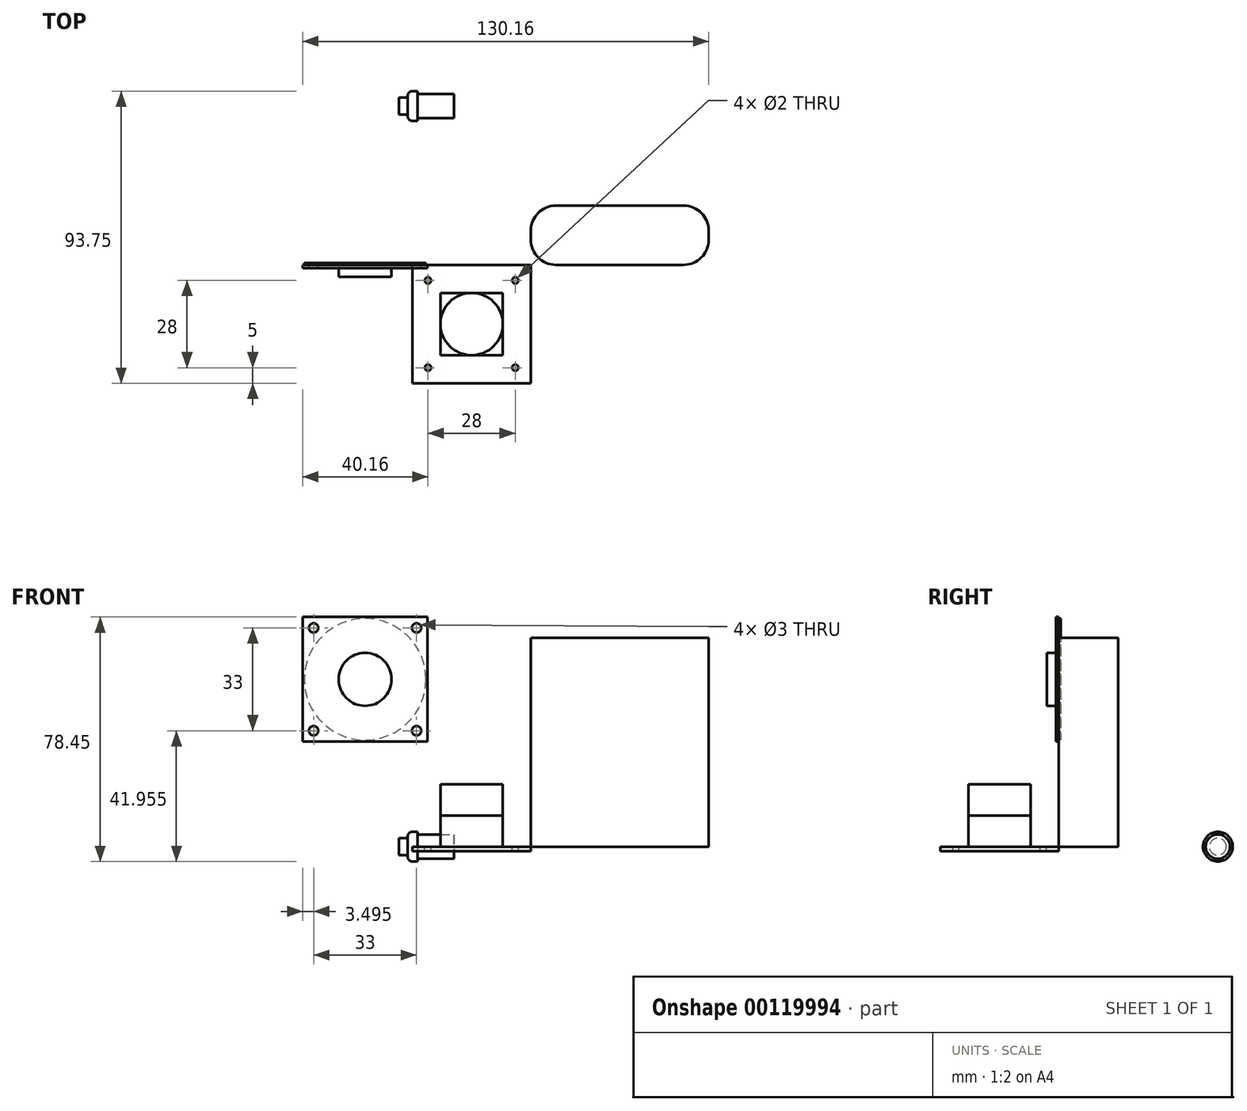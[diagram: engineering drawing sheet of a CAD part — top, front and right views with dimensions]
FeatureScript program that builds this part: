
annotation { "Feature Type Name" : "Feature", "Feature Type Description" : "" }
export const myFeature = defineFeature(function(context is Context, id is Id, definition is map)
    precondition{}
    {
        {
            var Q0;
            Q0=qCreatedBy(makeId("Top.planeOp"),FACE);
            var sketch = newSketch(context, id + "F0", { "sketchPlane" : qUnion([Q0])});
            skLineSegment(sketch, "E0.bottom", {"start": v(8, 0) * mm, "end": v(49, 0) * mm});
            skLineSegment(sketch, "E0.top", {"start": v(8, 19) * mm, "end": v(49, 19) * mm});
            skLineSegment(sketch, "E0.left", {"start": v(0, 8) * mm, "end": v(0, 11) * mm});
            skLineSegment(sketch, "E0.right", {"start": v(57, 8) * mm, "end": v(57, 11) * mm});
            skPoint(sketch, "E1.visualSharp", {"position": v(0, 19) * mm});
            skArc(sketch, "E1.filletArc", {"start": v(8, 19) * mm, "mid": v(2.34, 16.66) * mm, "end": v(0, 11) * mm});
            skPoint(sketch, "E2.visualSharp", {"position": v(0, 0) * mm});
            skArc(sketch, "E2.filletArc", {"start": v(0, 8) * mm, "mid": v(2.34, 2.34) * mm, "end": v(8, 0) * mm});
            skPoint(sketch, "E3.visualSharp", {"position": v(57, 19) * mm});
            skArc(sketch, "E3.filletArc", {"start": v(57, 11) * mm, "mid": v(54.66, 16.66) * mm, "end": v(49, 19) * mm});
            skPoint(sketch, "E4.visualSharp", {"position": v(57, 0) * mm});
            skArc(sketch, "E4.filletArc", {"start": v(49, 0) * mm, "mid": v(54.66, 2.34) * mm, "end": v(57, 8) * mm});
            skSolve(sketch);
        }
        {
            var Q0;
            Q0=makeQuery(id+"F0.imprint","IMPRINT",FACE,{"disambiguationData":[TD([[makeQuery(id+"F0.imprint","IMPRINT",EDGE,{"derivedFrom":sQuery(id+"F0.wireOp",EDGE,"E0.bottom")}),1.0]])]});
            extrude(context, id + "F1", {"entities" : qUnion([Q0]), "depth" : 67 * mm});
        }
        {
            var Q0;
            Q0=qCreatedBy(makeId("Top.planeOp"),FACE);
            var sketch = newSketch(context, id + "F2", { "sketchPlane" : qUnion([Q0])});
            skLineSegment(sketch, "E5.bottom", {"start": v(0, 0) * mm, "end": v(-38, 0) * mm});
            skLineSegment(sketch, "E5.top", {"start": v(0, -38) * mm, "end": v(-38, -38) * mm});
            skLineSegment(sketch, "E5.left", {"start": v(0, 0) * mm, "end": v(0, -38) * mm});
            skLineSegment(sketch, "E5.right", {"start": v(-38, 0) * mm, "end": v(-38, -38) * mm});
            skLineSegment(sketch, "E6.bottom", {"start": v(-33, -5) * mm, "end": v(-5, -5) * mm, "construction": true});
            skLineSegment(sketch, "E6.top", {"start": v(-33, -33) * mm, "end": v(-5, -33) * mm, "construction": true});
            skLineSegment(sketch, "E6.left", {"start": v(-33, -5) * mm, "end": v(-33, -33) * mm, "construction": true});
            skLineSegment(sketch, "E6.right", {"start": v(-5, -5) * mm, "end": v(-5, -33) * mm, "construction": true});
            skPoint(sketch, "E6.middle", {"position": v(-19, -19) * mm});
            skPoint(sketch, "E6.middle.positionSnap0", {"position": v(-19, -38) * mm});
            skPoint(sketch, "E6.middle.positionSnap1", {"position": v(0, -19) * mm});
            skPoint(sketch, "E6.centerSnap0", {"position": v(-19, -38) * mm});
            skPoint(sketch, "E6.centerSnap1", {"position": v(0, -19) * mm});
            skLineSegment(sketch, "E7.bottom", {"start": v(-29, -9) * mm, "end": v(-9, -9) * mm});
            skLineSegment(sketch, "E7.top", {"start": v(-29, -29) * mm, "end": v(-9, -29) * mm});
            skLineSegment(sketch, "E7.left", {"start": v(-29, -9) * mm, "end": v(-29, -29) * mm});
            skLineSegment(sketch, "E7.right", {"start": v(-9, -9) * mm, "end": v(-9, -29) * mm});
            skCircle(sketch, "E8", {"center": v(-33, -5) * mm, "radius": 1 * mm});
            skCircle(sketch, "E9", {"center": v(-5, -5) * mm, "radius": 1 * mm});
            skCircle(sketch, "E10", {"center": v(-5, -33) * mm, "radius": 1 * mm});
            skCircle(sketch, "E11", {"center": v(-33, -33) * mm, "radius": 1 * mm});
            skCircle(sketch, "E12", {"center": v(-19, -19) * mm, "radius": 10 * mm});
            skSolve(sketch);
        }
        {
            var Q0;
            Q0 = qSketchRegion(id + "F2", true);
            var Q1;
            Q1=makeQuery(id+"F2.imprint","IMPRINT",FACE,{"disambiguationData":[TD([[makeQuery(id+"F2.imprint","IMPRINT",EDGE,{"derivedFrom":sQuery(id+"F2.wireOp",EDGE,"E7.bottom")}),-1.0]])]});
            var Q2;
            {var subQ0=sQuery(id+"F2.wireOp",EDGE,"E12");var subQ1=makeQuery(id+"F2.imprint","INTERSECT",VERTEX,{"derivedFrom":[sQuery(id+"F2.wireOp",EDGE,"E7.bottom"),subQ0]});Q2=makeQuery(id+"F2.imprint","IMPRINT",FACE,{"disambiguationData":[TD([[makeQuery(id+"F2.imprint","IMPRINT",EDGE,{"disambiguationData":[TD([[subQ1,1.0]])],"derivedFrom":subQ0}),1.0]])]});}
            var Q3;
            {var subQ0=sQuery(id+"F2.wireOp",EDGE,"E7.left");var subQ1=sQuery(id+"F2.wireOp",EDGE,"E7.top");var subQ2=makeQuery(id+"F2.imprint","INTERSECT",VERTEX,{"derivedFrom":[subQ1,subQ0]});Q3=makeQuery(id+"F2.imprint","IMPRINT",FACE,{"disambiguationData":[TD([[makeQuery(id+"F2.imprint","IMPRINT",EDGE,{"disambiguationData":[TD([[subQ2,-1.0]])],"derivedFrom":subQ1}),1.0]])]});}
            var Q4;
            {var subQ0=sQuery(id+"F2.wireOp",EDGE,"E7.right");var subQ1=sQuery(id+"F2.wireOp",EDGE,"E7.top");var subQ2=makeQuery(id+"F2.imprint","INTERSECT",VERTEX,{"derivedFrom":[subQ1,subQ0]});Q4=makeQuery(id+"F2.imprint","IMPRINT",FACE,{"disambiguationData":[TD([[makeQuery(id+"F2.imprint","IMPRINT",EDGE,{"disambiguationData":[TD([[subQ2,1.0]])],"derivedFrom":subQ1}),1.0]])]});}
            extrude(context, id + "F3", {"entities" : qUnion([Q0, Q1, Q2, Q3, Q4]), "oppositeDirection" : true, "depth" : 1.5 * mm});
        }
        {
            var Q0;
            Q0=makeQuery(id+"F2.imprint","IMPRINT",FACE,{"disambiguationData":[TD([[makeQuery(id+"F2.imprint","IMPRINT",EDGE,{"derivedFrom":sQuery(id+"F2.wireOp",EDGE,"E7.bottom")}),-1.0]])]});
            var Q1;
            {var subQ0=sQuery(id+"F2.wireOp",EDGE,"E7.left");var subQ1=sQuery(id+"F2.wireOp",EDGE,"E7.top");var subQ2=makeQuery(id+"F2.imprint","INTERSECT",VERTEX,{"derivedFrom":[subQ1,subQ0]});Q1=makeQuery(id+"F2.imprint","IMPRINT",FACE,{"disambiguationData":[TD([[makeQuery(id+"F2.imprint","IMPRINT",EDGE,{"disambiguationData":[TD([[subQ2,-1.0]])],"derivedFrom":subQ1}),1.0]])]});}
            var Q2;
            {var subQ0=sQuery(id+"F2.wireOp",EDGE,"E12");var subQ1=makeQuery(id+"F2.imprint","INTERSECT",VERTEX,{"derivedFrom":[sQuery(id+"F2.wireOp",EDGE,"E7.bottom"),subQ0]});Q2=makeQuery(id+"F2.imprint","IMPRINT",FACE,{"disambiguationData":[TD([[makeQuery(id+"F2.imprint","IMPRINT",EDGE,{"disambiguationData":[TD([[subQ1,1.0]])],"derivedFrom":subQ0}),1.0]])]});}
            var Q3;
            {var subQ0=sQuery(id+"F2.wireOp",EDGE,"E7.right");var subQ1=sQuery(id+"F2.wireOp",EDGE,"E7.top");var subQ2=makeQuery(id+"F2.imprint","INTERSECT",VERTEX,{"derivedFrom":[subQ1,subQ0]});Q3=makeQuery(id+"F2.imprint","IMPRINT",FACE,{"disambiguationData":[TD([[makeQuery(id+"F2.imprint","IMPRINT",EDGE,{"disambiguationData":[TD([[subQ2,1.0]])],"derivedFrom":subQ1}),1.0]])]});}
            extrude(context, id + "F4", {"entities" : qUnion([Q0, Q1, Q2, Q3]), "operationType" : NewBodyOperationType.ADD, "depth" : 10 * mm});
        }
        {
            var Q0;
            {var subQ0=sQuery(id+"F2.wireOp",EDGE,"E12");var subQ1=makeQuery(id+"F2.imprint","INTERSECT",VERTEX,{"derivedFrom":[sQuery(id+"F2.wireOp",EDGE,"E7.bottom"),subQ0]});Q0=makeQuery(id+"F2.imprint","IMPRINT",FACE,{"disambiguationData":[TD([[makeQuery(id+"F2.imprint","IMPRINT",EDGE,{"disambiguationData":[TD([[subQ1,1.0]])],"derivedFrom":subQ0}),1.0]])]});}
            extrude(context, id + "F5", {"entities" : qUnion([Q0]), "operationType" : NewBodyOperationType.ADD, "depth" : 20 * mm});
        }
        {
            var Q0;
            Q0=qCreatedBy(makeId("Front.planeOp"),FACE);
            var sketch = newSketch(context, id + "F6", { "sketchPlane" : qUnion([Q0])});
            skLineSegment(sketch, "E13.bottom", {"start": v(-73.16, 73.67) * mm, "end": v(-33.16, 73.67) * mm});
            skLineSegment(sketch, "E13.top", {"start": v(-73.16, 33.67) * mm, "end": v(-33.16, 33.67) * mm});
            skLineSegment(sketch, "E13.left", {"start": v(-73.16, 73.67) * mm, "end": v(-73.16, 33.67) * mm});
            skLineSegment(sketch, "E13.right", {"start": v(-33.16, 73.67) * mm, "end": v(-33.16, 33.67) * mm});
            skLineSegment(sketch, "E14.bottom", {"start": v(-69.66, 70.17) * mm, "end": v(-36.66, 70.17) * mm, "construction": true});
            skLineSegment(sketch, "E14.top", {"start": v(-69.66, 37.17) * mm, "end": v(-36.66, 37.17) * mm, "construction": true});
            skLineSegment(sketch, "E14.left", {"start": v(-69.66, 70.17) * mm, "end": v(-69.66, 37.17) * mm, "construction": true});
            skLineSegment(sketch, "E14.right", {"start": v(-36.66, 70.17) * mm, "end": v(-36.66, 37.17) * mm, "construction": true});
            skPoint(sketch, "E14.middle", {"position": v(-53.16, 53.67) * mm});
            skPoint(sketch, "E14.middle.positionSnap0", {"position": v(-53.16, 73.67) * mm});
            skPoint(sketch, "E14.middle.positionSnap1", {"position": v(-73.16, 53.67) * mm});
            skPoint(sketch, "E14.centerSnap0", {"position": v(-53.16, 73.67) * mm});
            skPoint(sketch, "E14.centerSnap1", {"position": v(-73.16, 53.67) * mm});
            skPoint(sketch, "E15", {"position": v(-69.66, 70.17) * mm});
            skPoint(sketch, "E16", {"position": v(-36.66, 70.17) * mm});
            skPoint(sketch, "E17", {"position": v(-36.66, 37.17) * mm});
            skPoint(sketch, "E18", {"position": v(-69.66, 37.17) * mm});
            skCircle(sketch, "E19", {"center": v(-53.16, 53.67) * mm, "radius": 19.5 * mm});
            skCircle(sketch, "E20", {"center": v(-53.16, 53.67) * mm, "radius": 8.5 * mm});
            skSolve(sketch);
        }
        {
            var Q0;
            Q0=makeQuery(id+"F6.imprint","IMPRINT",FACE,{"disambiguationData":[TD([[makeQuery(id+"F6.imprint","IMPRINT",EDGE,{"derivedFrom":sQuery(id+"F6.wireOp",EDGE,"E19")}),1.0]])]});
            var Q1;
            Q1=makeQuery(id+"F6.imprint","IMPRINT",FACE,{"disambiguationData":[TD([[makeQuery(id+"F6.imprint","IMPRINT",EDGE,{"derivedFrom":sQuery(id+"F6.wireOp",EDGE,"E20")}),1.0]])]});
            var Q2;
            Q2=makeQuery(id+"F6.imprint","IMPRINT",FACE,{"disambiguationData":[TD([[makeQuery(id+"F6.imprint","IMPRINT",EDGE,{"derivedFrom":sQuery(id+"F6.wireOp",EDGE,"E13.bottom")}),-1.0]])]});
            extrude(context, id + "F7", {"entities" : qUnion([Q0, Q1, Q2]), "depth" : 1 * mm});
        }
        {
            var Q0;
            Q0=makeQuery(id+"F6.imprint","IMPRINT",FACE,{"disambiguationData":[TD([[makeQuery(id+"F6.imprint","IMPRINT",EDGE,{"derivedFrom":sQuery(id+"F6.wireOp",EDGE,"E20")}),1.0]])]});
            var Q1;
            Q1=makeQuery(id+"F6.imprint","IMPRINT",FACE,{"disambiguationData":[TD([[makeQuery(id+"F6.imprint","IMPRINT",EDGE,{"derivedFrom":sQuery(id+"F6.wireOp",EDGE,"E19")}),1.0]])]});
            extrude(context, id + "F8", {"entities" : qUnion([Q0, Q1]), "operationType" : NewBodyOperationType.ADD, "oppositeDirection" : true, "depth" : 0.6 * mm});
        }
        {
            var Q0;
            Q0=makeQuery(id+"F6.imprint","IMPRINT",FACE,{"disambiguationData":[TD([[makeQuery(id+"F6.imprint","IMPRINT",EDGE,{"derivedFrom":sQuery(id+"F6.wireOp",EDGE,"E20")}),1.0]])]});
            extrude(context, id + "F9", {"entities" : qUnion([Q0]), "operationType" : NewBodyOperationType.ADD, "depth" : 3.9 * mm});
        }
        {
            var Q0;
            Q0=sQuery(id+"F6.wireOp",VERTEX,"E15");
            var Q1;
            Q1=sQuery(id+"F6.wireOp",VERTEX,"E18");
            var Q2;
            Q2=sQuery(id+"F6.wireOp",VERTEX,"E17");
            var Q3;
            Q3=sQuery(id+"F6.wireOp",VERTEX,"E16");
            var Q4;
            Q4=makeQuery(id+"F7.opExtrude","SWEPT_BODY",BODY,{"disambiguationData":[OSD([sQuery(id+"F6.wireOp",EDGE,"E13.bottom"),sQuery(id+"F6.wireOp",EDGE,"E13.top"),sQuery(id+"F6.wireOp",EDGE,"E13.left"),sQuery(id+"F6.wireOp",EDGE,"E13.right")])]});
            hole(context, id + "F10", {"style" : HoleStyle.SIMPLE, "endStyle" : HoleEndStyle.THROUGH, "oppositeDirection" : true, "holeDiameter" : 3 * mm, "locations" : qUnion([Q0, Q1, Q2, Q3]), "scope" : qUnion([Q4]), "isTappedThrough" : true});
        }
        {
            var Q0;
            Q0=qCreatedBy(makeId("Top.planeOp"),FACE);
            var sketch = newSketch(context, id + "F11", { "sketchPlane" : qUnion([Q0])});
            skLineSegment(sketch, "E21", {"start": v(-24.67, 50.98) * mm, "end": v(-42.31, 50.98) * mm});
            skLineSegment(sketch, "E22", {"start": v(-42.31, 50.98) * mm, "end": v(-42.31, 53.68) * mm});
            skLineSegment(sketch, "E23", {"start": v(-42.31, 53.68) * mm, "end": v(-39.52, 53.68) * mm});
            skLineSegment(sketch, "E24", {"start": v(-39.52, 53.68) * mm, "end": v(-39.52, 54.25) * mm});
            skLineSegment(sketch, "E25", {"start": v(-38.02, 55.75) * mm, "end": v(-36.31, 55.75) * mm});
            skLineSegment(sketch, "E26", {"start": v(-36.31, 55.75) * mm, "end": v(-36.31, 54.88) * mm});
            skLineSegment(sketch, "E27", {"start": v(-36.31, 54.88) * mm, "end": v(-24.67, 54.88) * mm});
            skLineSegment(sketch, "E28", {"start": v(-24.67, 54.88) * mm, "end": v(-24.67, 50.98) * mm});
            skPoint(sketch, "E29.visualSharp", {"position": v(-39.52, 55.75) * mm});
            skArc(sketch, "E29.filletArc", {"start": v(-38.02, 55.75) * mm, "mid": v(-39.08, 55.31) * mm, "end": v(-39.52, 54.25) * mm});
            skLineSegment(sketch, "E30.MirrorCS", {"start": v(-42.31, 50.98) * mm, "end": v(-42.31, 48.28) * mm, "construction": true});
            skLineSegment(sketch, "E31.MirrorCS", {"start": v(-42.31, 48.28) * mm, "end": v(-39.52, 48.28) * mm, "construction": true});
            skLineSegment(sketch, "E32.MirrorCS", {"start": v(-39.52, 48.28) * mm, "end": v(-39.52, 47.7) * mm, "construction": true});
            skArc(sketch, "E33.MirrorCS", {"start": v(-38.02, 46.2) * mm, "mid": v(-39.08, 46.64) * mm, "end": v(-39.52, 47.7) * mm, "construction": true});
            skLineSegment(sketch, "E34.MirrorCS", {"start": v(-38.02, 46.2) * mm, "end": v(-36.31, 46.2) * mm, "construction": true});
            skLineSegment(sketch, "E35.MirrorCS", {"start": v(-36.31, 46.2) * mm, "end": v(-36.31, 47.08) * mm, "construction": true});
            skLineSegment(sketch, "E36.MirrorCS", {"start": v(-36.31, 47.08) * mm, "end": v(-24.67, 47.08) * mm, "construction": true});
            skLineSegment(sketch, "E37.MirrorCS", {"start": v(-24.67, 47.08) * mm, "end": v(-24.67, 50.98) * mm, "construction": true});
            skSolve(sketch);
        }
        {
            var Q0;
            Q0=makeQuery(id+"F11.imprint","IMPRINT",FACE,{"disambiguationData":[TD([[makeQuery(id+"F11.imprint","IMPRINT",EDGE,{"derivedFrom":sQuery(id+"F11.wireOp",EDGE,"E21")}),-1.0]])]});
            var Q1;
            Q1=sQuery(id+"F11.wireOp",EDGE,"E21");
            revolve(context, id + "F12", {"entities" : qUnion([Q0]), "axis" : qUnion([Q1]), "revolveType" : RevolveType.FULL});
        }
    });
